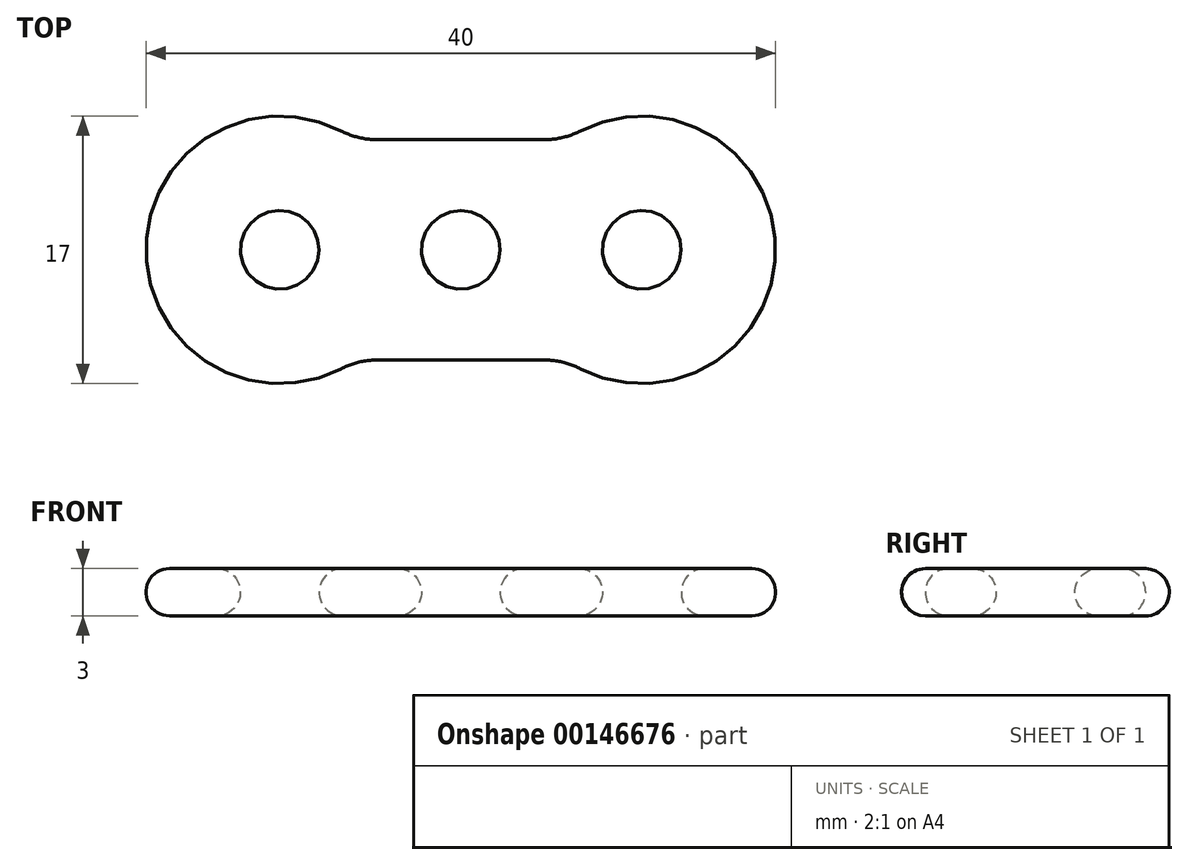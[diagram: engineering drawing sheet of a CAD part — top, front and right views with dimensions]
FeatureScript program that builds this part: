
annotation { "Feature Type Name" : "Feature", "Feature Type Description" : "" }
export const myFeature = defineFeature(function(context is Context, id is Id, definition is map)
    precondition{}
    {
        {
            var Q0;
            Q0=qCreatedBy(makeId("Top.planeOp"),FACE);
            var sketch = newSketch(context, id + "F0", { "sketchPlane" : qUnion([Q0])});
            skCircle(sketch, "E0", {"center": v(-11.5, 0) * mm, "radius": 2.5 * mm});
            skCircle(sketch, "E1.MirrorC", {"center": v(11.5, 0) * mm, "radius": 2.5 * mm});
            skCircle(sketch, "E2", {"center": v(0, 0) * mm, "radius": 2.5 * mm});
            skArc(sketch, "E3", {"start": v(-7.6, 7.56) * mm, "mid": v(-20, 0) * mm, "end": v(-7.6, -7.56) * mm});
            skArc(sketch, "E4.filletArc", {"start": v(-7.6, 7.56) * mm, "mid": v(-6.5, 7.14) * mm, "end": v(-5.32, 7) * mm});
            skArc(sketch, "E5.filletArc", {"start": v(-5.32, -7) * mm, "mid": v(-6.5, -7.14) * mm, "end": v(-7.6, -7.56) * mm});
            skArc(sketch, "E6.MirrorCS", {"start": v(7.6, 7.56) * mm, "mid": v(20, 0) * mm, "end": v(7.6, -7.56) * mm});
            skArc(sketch, "E7.MirrorCS", {"start": v(5.32, -7) * mm, "mid": v(6.5, -7.14) * mm, "end": v(7.6, -7.56) * mm});
            skArc(sketch, "E8.MirrorCS", {"start": v(7.6, 7.56) * mm, "mid": v(6.5, 7.14) * mm, "end": v(5.32, 7) * mm});
            skLineSegment(sketch, "E9", {"start": v(-5.32, 7) * mm, "end": v(5.32, 7) * mm});
            skLineSegment(sketch, "E10", {"start": v(-5.32, -7) * mm, "end": v(5.32, -7) * mm});
            skSolve(sketch);
        }
        {
            var Q0;
            Q0 = qSketchRegion(id + "F0", true);
            extrude(context, id + "F1", {"entities" : qUnion([Q0]), "depth" : 3 * mm});
        }
        {
            var Q0;
            Q0=makeQuery(id+"F1.opExtrude","CAP_EDGE",EDGE,{"disambiguationData":[OSD([sQuery(id+"F0.wireOp",EDGE,"lF0VukA9-KT6N-gBFH-iM43-Fj5hEu0lMzGX"),sQuery(id+"F0.wireOp",EDGE,"7161df79-24e9-4428-b099-f8e7b67f35541.MirrorCS")])],"isStart":false});
            var Q1;
            Q1=makeQuery(id+"F1.opExtrude","CAP_EDGE",EDGE,{"disambiguationData":[OSD([sQuery(id+"F0.wireOp",EDGE,"3KjJByLM-kuFr-jhpE-fLOg-5nn8W6Xfto6K"),sQuery(id+"F0.wireOp",EDGE,"7161df79-24e9-4428-b099-f8e7b67f35542.MirrorCS")])],"isStart":true});
            var Q2;
            Q2=makeQuery(id+"F1.opExtrude","CAP_EDGE",EDGE,{"disambiguationData":[OSD([sQuery(id+"F0.wireOp",EDGE,"E0")])],"isStart":false});
            var Q3;
            Q3=makeQuery(id+"F1.opExtrude","CAP_EDGE",EDGE,{"disambiguationData":[OSD([sQuery(id+"F0.wireOp",EDGE,"E2")])],"isStart":false});
            var Q4;
            Q4=makeQuery(id+"F1.opExtrude","CAP_EDGE",EDGE,{"disambiguationData":[OSD([sQuery(id+"F0.wireOp",EDGE,"E1.MirrorC")])],"isStart":false});
            var Q5;
            Q5=makeQuery(id+"F1.opExtrude","CAP_EDGE",EDGE,{"disambiguationData":[OSD([sQuery(id+"F0.wireOp",EDGE,"E1.MirrorC")])],"isStart":true});
            var Q6;
            Q6=makeQuery(id+"F1.opExtrude","CAP_EDGE",EDGE,{"disambiguationData":[OSD([sQuery(id+"F0.wireOp",EDGE,"E2")])],"isStart":true});
            var Q7;
            Q7=makeQuery(id+"F1.opExtrude","CAP_EDGE",EDGE,{"disambiguationData":[OSD([sQuery(id+"F0.wireOp",EDGE,"E0")])],"isStart":true});
            var Q8;
            Q8=makeQuery(id+"F1.opExtrude","CAP_EDGE",EDGE,{"disambiguationData":[OSD([sQuery(id+"F0.wireOp",EDGE,"E3")])],"isStart":false});
            var Q9;
            Q9=makeQuery(id+"F1.opExtrude","CAP_EDGE",EDGE,{"disambiguationData":[OSD([sQuery(id+"F0.wireOp",EDGE,"E5.filletArc")])],"isStart":true});
            fillet(context, id + "F2", {"entities" : qUnion([Q0, Q1, Q2, Q3, Q4, Q5, Q6, Q7, Q8, Q9]), "radius" : 1.5 * mm, "tangentPropagation" : true, "allowEdgeOverflow" : false});
        }
    });
